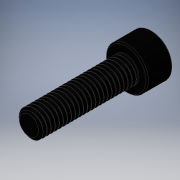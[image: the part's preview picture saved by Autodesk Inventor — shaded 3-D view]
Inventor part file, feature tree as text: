
AUTODESK INVENTOR PART (.ipt)
format: ipt  version: 2016 (Build 200138000, 138)  size: 797,696 bytes
history: native  units: in
note: dims shown in document units (in); Inventor stores cm internally (conversion verified against a paired STEP export)
features: revolve x1
ambient origin geometry x8: Origin, YZ Plane, XZ Plane, XY Plane, X Axis, Y Axis, Z Axis, Center Point
bodies: Solid1 (feature_tree)
feature tree (1):
  revolve  "Revolve1"  [1 undecoded]
note: 1 required parameter value undecoded (feature->parameter linkage not recoverable at this tier; creation-order binding heuristic only, values carry confidence <= 0.55)
